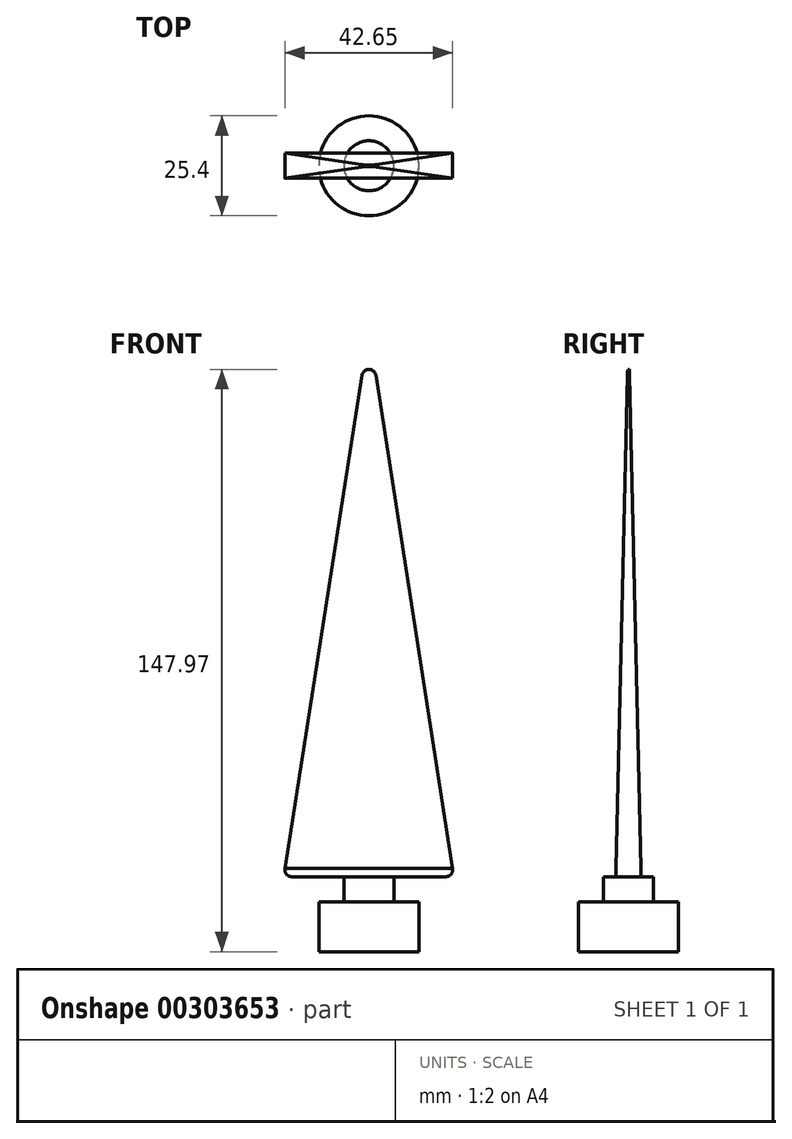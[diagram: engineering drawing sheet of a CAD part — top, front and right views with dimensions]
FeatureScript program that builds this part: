
annotation { "Feature Type Name" : "Feature", "Feature Type Description" : "" }
export const myFeature = defineFeature(function(context is Context, id is Id, definition is map)
    precondition{}
    {
        {
            var Q0;
            Q0=qCreatedBy(makeId("Front.planeOp"),FACE);
            var sketch = newSketch(context, id + "F0", { "sketchPlane" : qUnion([Q0])});
            skLineSegment(sketch, "E0", {"start": v(-20.18, -75.13) * mm, "end": v(-20.18, -62.43) * mm});
            skLineSegment(sketch, "E1", {"start": v(-20.18, -62.43) * mm, "end": v(5.22, -62.43) * mm});
            skLineSegment(sketch, "E2", {"start": v(5.22, -62.43) * mm, "end": v(5.22, -75.13) * mm});
            skLineSegment(sketch, "E3", {"start": v(-1.13, -62.43) * mm, "end": v(-1.13, -56.08) * mm});
            skLineSegment(sketch, "E4", {"start": v(-13.83, -62.43) * mm, "end": v(-13.83, -56.08) * mm});
            skLineSegment(sketch, "E5", {"start": v(-13.83, -56.08) * mm, "end": v(-1.13, -56.08) * mm});
            skLineSegment(sketch, "E6", {"start": v(-13.83, -56.08) * mm, "end": v(-29.14, -56.08) * mm});
            skLineSegment(sketch, "E7", {"start": v(-1.13, -56.08) * mm, "end": v(14.11, -56.08) * mm});
            skLineSegment(sketch, "E8", {"start": v(-29.14, -56.08) * mm, "end": v(-7.48, 82.6) * mm});
            skPoint(sketch, "E8.endSnap0", {"position": v(-7.48, -56.08) * mm});
            skLineSegment(sketch, "E9", {"start": v(-7.48, 82.6) * mm, "end": v(14.11, -56.08) * mm});
            skLineSegment(sketch, "E10", {"start": v(-20.18, -75.13) * mm, "end": v(5.22, -75.13) * mm});
            skLineSegment(sketch, "E11", {"start": v(-7.48, -56.08) * mm, "end": v(-7.48, -75.13) * mm});
            skLineSegment(sketch, "E12", {"start": v(-29.14, -56.08) * mm, "end": v(14.11, -56.08) * mm});
            skSolve(sketch);
        }
        {
            var Q0;
            {var subQ4=sQuery(id+"F0.wireOp",EDGE,"E0");Q0=makeQuery(id+"F0.imprint","IMPRINT",FACE,{"disambiguationData":[TD([[makeQuery(id+"F0.imprint","IMPRINT",EDGE,{"derivedFrom":subQ4}),-1.0]])]});}
            var Q1;
            {var subQ0=sQuery(id+"F0.wireOp",EDGE,"E3");Q1=makeQuery(id+"F0.imprint","IMPRINT",FACE,{"disambiguationData":[TD([[makeQuery(id+"F0.imprint","IMPRINT",EDGE,{"derivedFrom":subQ0}),1.0]])]});}
            var Q2;
            Q2=sQuery(id+"F0.wireOp",EDGE,"E11");
            revolve(context, id + "F1", {"entities" : qUnion([Q0, Q1]), "axis" : qUnion([Q2]), "revolveType" : RevolveType.FULL});
        }
        {
            var Q0;
            {var subQ3=sQuery(id+"F0.wireOp",EDGE,"E8");Q0=makeQuery(id+"F0.imprint","IMPRINT",FACE,{"disambiguationData":[TD([[makeQuery(id+"F0.imprint","IMPRINT",EDGE,{"derivedFrom":subQ3}),-1.0]])]});}
            extrude(context, id + "F2", {"entities" : qUnion([Q0]), "endBound" : BoundingType.SYMMETRIC, "depth" : 6.35 * mm});
        }
        {
            var Q0;
            Q0=makeQuery(id+"F2.opExtrude","SWEPT_EDGE",EDGE,{"disambiguationData":[OSD([sQuery(id+"F0.wireOp",EDGE,"E8"),sQuery(id+"F0.wireOp",EDGE,"E12")])]});
            var Q1;
            Q1=makeQuery(id+"F2.opExtrude","SWEPT_EDGE",EDGE,{"disambiguationData":[OSD([sQuery(id+"F0.wireOp",EDGE,"E9"),sQuery(id+"F0.wireOp",EDGE,"E12")])]});
            fillet(context, id + "F3", {"entities" : qUnion([Q0, Q1]), "radius" : 1.78 * mm, "tangentPropagation" : true, "allowEdgeOverflow" : false});
        }
        {
            var Q0;
            Q0=qCreatedBy(makeId("Right.planeOp"),FACE);
            var sketch = newSketch(context, id + "F4", { "sketchPlane" : qUnion([Q0])});
            skLineSegment(sketch, "E13", {"start": v(-3.17, -54.03) * mm, "end": v(0, 82.6) * mm});
            skLineSegment(sketch, "E14", {"start": v(0, 82.6) * mm, "end": v(3.17, -54.03) * mm});
            skLineSegment(sketch, "E15.0.0", {"start": v(-3.18, 82.6) * mm, "end": v(-3.18, -54.03) * mm});
            skLineSegment(sketch, "E15.0.2", {"start": v(3.18, -54.03) * mm, "end": v(3.18, 82.6) * mm});
            skLineSegment(sketch, "E15.0.3", {"start": v(3.17, 82.6) * mm, "end": v(-3.18, 82.6) * mm});
            skSolve(sketch);
        }
        {
            var Q0;
            Q0 = qSketchRegion(id + "F4", true);
            extrude(context, id + "F5", {"entities" : qUnion([Q0]), "operationType" : NewBodyOperationType.REMOVE, "endBound" : BoundingType.SYMMETRIC, "oppositeDirection" : true, "depth" : 63.5 * mm});
        }
    });
